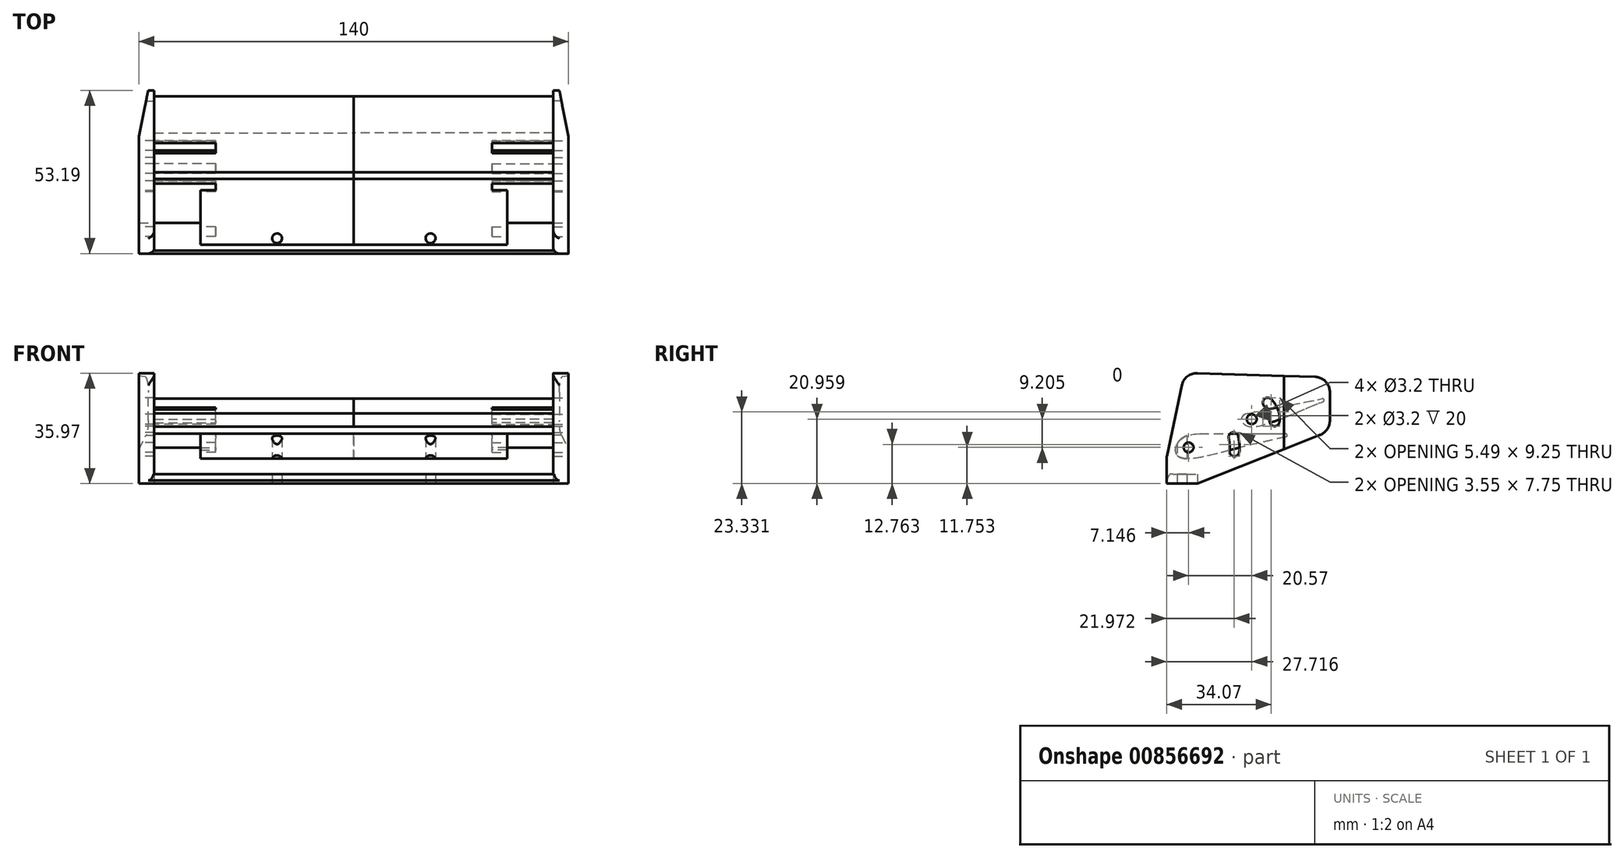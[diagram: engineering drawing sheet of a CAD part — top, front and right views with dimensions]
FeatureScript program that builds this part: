
annotation { "Feature Type Name" : "Feature", "Feature Type Description" : "" }
export const myFeature = defineFeature(function(context is Context, id is Id, definition is map)
    precondition{}
    {
        {
            var Q0;
            Q0=qCreatedBy(makeId("Right.planeOp"),FACE);
            var sketch = newSketch(context, id + "F0", { "sketchPlane" : qUnion([Q0])});
            skFitSpline(sketch, "E0", {"points": [v(0, 15) * mm, v(-15.97, 11.3) * mm, v(-26.3, 8.63) * mm, v(-36.38, 6.87) * mm, v(-40, 8.6) * mm, v(-38.45, 13.22) * mm, v(-32.23, 15) * mm], "startDerivative": vector(-50.3, -12.86) * mm, "endDerivative": vector(44.03, 0) * mm});
            skLineSegment(sketch, "E1", {"start": v(-32.23, 15) * mm, "end": v(-4.23, 15) * mm});
            skArc(sketch, "E2.filletArc", {"start": v(-4.11, 14.01) * mm, "mid": v(-3.73, 14.56) * mm, "end": v(-4.23, 15) * mm});
            skSolve(sketch);
        }
        {
            var Q0;
            Q0 = qSketchRegion(id + "F0", true);
            extrude(context, id + "F1", {"entities" : qUnion([Q0]), "depth" : 65 * mm, "offsetDistance" : 25 * mm});
        }
        {
            var Q0;
            Q0=makeQuery(id+"F1.opExtrude","CAP_FACE",FACE,{"disambiguationData":[OSD([sQuery(id+"F0.wireOp",EDGE,"E0"),sQuery(id+"F0.wireOp",EDGE,"E1"),sQuery(id+"F0.wireOp",EDGE,"E2.filletArc")])],"isStart":false});
            var sketch = newSketch(context, id + "F2", { "sketchPlane" : qUnion([Q0])});
            skCircle(sketch, "E3", {"center": v(-35.87, 10.53) * mm, "radius": 1.5 * mm});
            skSolve(sketch);
        }
        {
            var Q0;
            Q0 = qSketchRegion(id + "F2", true);
            extrude(context, id + "F3", {"entities" : qUnion([Q0]), "operationType" : NewBodyOperationType.REMOVE, "endBound" : BoundingType.SYMMETRIC, "oppositeDirection" : true, "depth" : 20 * mm, "offsetDistance" : 25 * mm});
        }
        {
            var Q0;
            Q0=qCreatedBy(makeId("Right.planeOp"),FACE);
            var sketch = newSketch(context, id + "F4", { "sketchPlane" : qUnion([Q0])});
            skLineSegment(sketch, "E4", {"start": v(-16.48, 21.66) * mm, "end": v(12.95, 27.47) * mm});
            skFitSpline(sketch, "E5", {"points": [v(-16.48, 21.66) * mm, v(-18.42, 20.57) * mm, v(-18.54, 19.05) * mm, v(-16.42, 17.47) * mm, v(-12.4, 17.65) * mm, v(-5.18, 20.08) * mm, v(4.36, 24.03) * mm, v(12.95, 27.47) * mm], "startDerivative": vector(-25.21, -3.34) * mm, "endDerivative": vector(44.37, 18.22) * mm});
            skSolve(sketch);
        }
        {
            var Q0;
            Q0 = qSketchRegion(id + "F4", true);
            extrude(context, id + "F5", {"entities" : qUnion([Q0]), "depth" : 65 * mm, "offsetDistance" : 25 * mm});
        }
        {
            var Q0;
            {var subQ0=sQuery(id+"F4.wireOp",EDGE,"E5");var subQ1=sQuery(id+"F4.wireOp",EDGE,"E4");Q0=makeQuery(id+"F5.opExtrude","SWEPT_EDGE",EDGE,{"disambiguationData":[OSD([subQ1,subQ0]),TDD([makeQuery(id+"F4.imprint","INTERSECT",VERTEX,{"disambiguationData":[OD(1.0)],"derivedFrom":[subQ1,subQ0]})])]});}
            fillet(context, id + "F6", {"entities" : qUnion([Q0]), "radius" : .5 * mm, "tangentPropagation" : true, "allowEdgeOverflow" : false});
        }
        {
            var Q0;
            Q0=makeQuery(id+"F5.opExtrude","CAP_FACE",FACE,{"disambiguationData":[OSD([sQuery(id+"F4.wireOp",EDGE,"E4"),sQuery(id+"F4.wireOp",EDGE,"E5")])],"isStart":false});
            var sketch = newSketch(context, id + "F7", { "sketchPlane" : qUnion([Q0])});
            skCircle(sketch, "E6", {"center": v(-15.3, 19.74) * mm, "radius": 1.5 * mm});
            skSolve(sketch);
        }
        {
            var Q0;
            Q0 = qSketchRegion(id + "F7", true);
            extrude(context, id + "F8", {"entities" : qUnion([Q0]), "operationType" : NewBodyOperationType.REMOVE, "endBound" : BoundingType.SYMMETRIC, "oppositeDirection" : true, "depth" : 15 * mm, "offsetDistance" : 25 * mm});
        }
        {
            var Q0;
            Q0=makeQuery(id+"F5.opExtrude","CAP_FACE",FACE,{"disambiguationData":[OSD([sQuery(id+"F4.wireOp",EDGE,"E4"),sQuery(id+"F4.wireOp",EDGE,"E5")])],"isStart":false});
            var sketch = newSketch(context, id + "F9", { "sketchPlane" : qUnion([Q0])});
            skLineSegment(sketch, "E7", {"start": v(-44.19, 1.78) * mm, "end": v(-33.46, 1.78) * mm});
            skLineSegment(sketch, "E8", {"start": v(-33.46, 1.78) * mm, "end": v(10.17, 15.63) * mm});
            skLineSegment(sketch, "E9", {"start": v(10.17, 15.63) * mm, "end": v(10.17, 33.4) * mm});
            skLineSegment(sketch, "E10", {"start": v(-39.8, 22.63) * mm, "end": v(-44.19, 1.78) * mm});
            skLineSegment(sketch, "E11", {"start": v(-39.8, 22.63) * mm, "end": v(-37.21, 34.88) * mm});
            skLineSegment(sketch, "E12", {"start": v(-37.21, 34.88) * mm, "end": v(10.17, 33.4) * mm});
            skSolve(sketch);
        }
        {
            var Q0;
            Q0 = qSketchRegion(id + "F9", true);
            extrude(context, id + "F10", {"entities" : qUnion([Q0]), "depth" : 5 * mm, "offsetDistance" : 25 * mm});
        }
        {
            var Q0;
            Q0=makeQuery(id+"F10.opExtrude","SWEPT_EDGE",EDGE,{"disambiguationData":[OSD([sQuery(id+"F9.wireOp",EDGE,"ADhL9wM5-Wbhb-7g79-Ji5l-QH4fZ3eOvgQA"),sQuery(id+"F9.wireOp",EDGE,"E10")])]});
            fillet(context, id + "F11", {"entities" : qUnion([Q0]), "radius" : 5 * mm, "tangentPropagation" : true, "allowEdgeOverflow" : false});
        }
        {
            var Q0;
            Q0=makeQuery(id+"F10.opExtrude","SWEPT_EDGE",EDGE,{"disambiguationData":[OSD([sQuery(id+"F9.wireOp",EDGE,"E9"),sQuery(id+"F9.wireOp",EDGE,"ADhL9wM5-Wbhb-7g79-Ji5l-QH4fZ3eOvgQA")])]});
            var Q1;
            Q1=makeQuery(id+"F10.opExtrude","SWEPT_EDGE",EDGE,{"disambiguationData":[OSD([sQuery(id+"F9.wireOp",EDGE,"E8"),sQuery(id+"F9.wireOp",EDGE,"E9")])]});
            var Q2;
            Q2=makeQuery(id+"F10.opExtrude","SWEPT_EDGE",EDGE,{"disambiguationData":[OSD([sQuery(id+"F9.wireOp",EDGE,"E7"),sQuery(id+"F9.wireOp",EDGE,"E8")])]});
            fillet(context, id + "F12", {"entities" : qUnion([Q0, Q1, Q2]), "radius" : 5 * mm, "tangentPropagation" : true, "allowEdgeOverflow" : false});
        }
        {
            var Q0;
            Q0=makeQuery(id+"F10.opExtrude","CAP_FACE",FACE,{"disambiguationData":[OSD([sQuery(id+"F9.wireOp",EDGE,"E7"),sQuery(id+"F9.wireOp",EDGE,"E8"),sQuery(id+"F9.wireOp",EDGE,"E9"),sQuery(id+"F9.wireOp",EDGE,"ADhL9wM5-Wbhb-7g79-Ji5l-QH4fZ3eOvgQA"),sQuery(id+"F9.wireOp",EDGE,"E10")])],"isStart":false});
            var sketch = newSketch(context, id + "F13", { "sketchPlane" : qUnion([Q0])});
            skCircle(sketch, "E13.0", {"center": v(-15.3, 19.74) * mm, "radius": 1.6 * mm});
            skArc(sketch, "E14", {"start": v(-8.98, 26.28) * mm, "mid": v(-11.25, 26.25) * mm, "end": v(-11.2, 23.98) * mm});
            skArc(sketch, "E15", {"start": v(-9.43, 19.22) * mm, "mid": v(-7.97, 17.49) * mm, "end": v(-6.24, 18.94) * mm});
            skArc(sketch, "E16", {"start": v(-9.43, 19.22) * mm, "mid": v(-9.78, 21.8) * mm, "end": v(-11.2, 23.98) * mm});
            skArc(sketch, "E17", {"start": v(-6.24, 18.94) * mm, "mid": v(-6.78, 22.92) * mm, "end": v(-8.98, 26.28) * mm});
            skSolve(sketch);
        }
        {
            var Q0;
            Q0 = qSketchRegion(id + "F13", true);
            extrude(context, id + "F14", {"entities" : qUnion([Q0]), "operationType" : NewBodyOperationType.REMOVE, "oppositeDirection" : true, "depth" : 25 * mm, "offsetDistance" : 25 * mm});
        }
        {
            var Q0;
            Q0=makeQuery(id+"F10.opExtrude","CAP_FACE",FACE,{"disambiguationData":[OSD([sQuery(id+"F9.wireOp",EDGE,"E7"),sQuery(id+"F9.wireOp",EDGE,"E8"),sQuery(id+"F9.wireOp",EDGE,"E9"),sQuery(id+"F9.wireOp",EDGE,"ADhL9wM5-Wbhb-7g79-Ji5l-QH4fZ3eOvgQA"),sQuery(id+"F9.wireOp",EDGE,"E10")])],"isStart":false});
            var sketch = newSketch(context, id + "F15", { "sketchPlane" : qUnion([Q0])});
            skCircle(sketch, "E18.0", {"center": v(-35.87, 10.53) * mm, "radius": 1.5 * mm, "construction": true});
            skCircle(sketch, "E19", {"center": v(-35.87, 10.53) * mm, "radius": 1.6 * mm});
            skArc(sketch, "E20", {"start": v(-19.68, 14.2) * mm, "mid": v(-21.6, 15.4) * mm, "end": v(-22.8, 13.49) * mm});
            skArc(sketch, "E21", {"start": v(-22.52, 9.4) * mm, "mid": v(-21.06, 7.67) * mm, "end": v(-19.33, 9.13) * mm});
            skArc(sketch, "E22", {"start": v(-22.52, 9.4) * mm, "mid": v(-22.5, 11.45) * mm, "end": v(-22.8, 13.49) * mm});
            skArc(sketch, "E23", {"start": v(-19.33, 9.13) * mm, "mid": v(-19.31, 11.67) * mm, "end": v(-19.68, 14.2) * mm});
            skSolve(sketch);
        }
        {
            var Q0;
            Q0 = qSketchRegion(id + "F15", true);
            extrude(context, id + "F16", {"entities" : qUnion([Q0]), "operationType" : NewBodyOperationType.REMOVE, "oppositeDirection" : true, "depth" : 25 * mm, "offsetDistance" : 25 * mm});
        }
        {
            var Q0;
            Q0=makeQuery(id+"F1.opExtrude","CAP_FACE",FACE,{"disambiguationData":[OSD([sQuery(id+"F0.wireOp",EDGE,"E0"),sQuery(id+"F0.wireOp",EDGE,"E1"),sQuery(id+"F0.wireOp",EDGE,"E2.filletArc")])],"isStart":false});
            var sketch = newSketch(context, id + "F17", { "sketchPlane" : qUnion([Q0])});
            skArc(sketch, "E24.0", {"start": v(-19.68, 14.2) * mm, "mid": v(-21.6, 15.4) * mm, "end": v(-22.8, 13.49) * mm});
            skCircle(sketch, "E25", {"center": v(-35.87, 10.53) * mm, "radius": 15 * mm});
            skCircle(sketch, "E26", {"center": v(-21.02, 12.64) * mm, "radius": 1.5 * mm});
            skSolve(sketch);
        }
        {
            var Q0;
            {var subQ0=sQuery(id+"F17.wireOp",EDGE,"E26");var subQ1=sQuery(id+"F17.wireOp",EDGE,"E25");var subQ2=makeQuery(id+"F17.imprint","INTERSECT",VERTEX,{"disambiguationData":[OD(0.0)],"derivedFrom":[subQ1,subQ0]});Q0=makeQuery(id+"F17.imprint","IMPRINT",FACE,{"disambiguationData":[TD([[makeQuery(id+"F17.imprint","IMPRINT",EDGE,{"disambiguationData":[TD([[subQ2,1.0]])],"derivedFrom":subQ1}),-1.0]])]});}
            var Q1;
            {var subQ0=sQuery(id+"F17.wireOp",EDGE,"E26");var subQ1=sQuery(id+"F17.wireOp",EDGE,"E25");var subQ2=makeQuery(id+"F17.imprint","INTERSECT",VERTEX,{"disambiguationData":[OD(0.0)],"derivedFrom":[subQ1,subQ0]});Q1=makeQuery(id+"F17.imprint","IMPRINT",FACE,{"disambiguationData":[TD([[makeQuery(id+"F17.imprint","IMPRINT",EDGE,{"disambiguationData":[TD([[subQ2,1.0]])],"derivedFrom":subQ1}),1.0]])]});}
            var Q2;
            Q2=sQuery(id+"F17.wireOp",EDGE,"E26");
            extrude(context, id + "F18", {"entities" : qUnion([Q0, Q1]), "operationType" : NewBodyOperationType.REMOVE, "surfaceEntities" : qUnion([Q2]), "oppositeDirection" : true, "depth" : 15 * mm, "offsetDistance" : 25 * mm});
        }
        {
            var Q0;
            Q0=makeQuery(id+"F5.opExtrude","CAP_FACE",FACE,{"disambiguationData":[OSD([sQuery(id+"F4.wireOp",EDGE,"E4"),sQuery(id+"F4.wireOp",EDGE,"E5")])],"isStart":false});
            var sketch = newSketch(context, id + "F19", { "sketchPlane" : qUnion([Q0])});
            skPoint(sketch, "E27.0", {"position": v(-11.25, 26.25) * mm});
            skCircle(sketch, "E28", {"center": v(-7.98, 21.37) * mm, "radius": 1.5 * mm});
            skSolve(sketch);
        }
        {
            var Q0;
            Q0 = qSketchRegion(id + "F19", true);
            extrude(context, id + "F20", {"entities" : qUnion([Q0]), "operationType" : NewBodyOperationType.REMOVE, "oppositeDirection" : true, "depth" : 15 * mm, "offsetDistance" : 25 * mm});
        }
        {
            var Q0;
            Q0=makeQuery(id+"F1.opExtrude","SWEPT_BODY",BODY,{"disambiguationData":[OSD([sQuery(id+"F0.wireOp",EDGE,"E0"),sQuery(id+"F0.wireOp",EDGE,"E1"),sQuery(id+"F0.wireOp",EDGE,"E2.filletArc")])]});
            var Q1;
            Q1=makeQuery(id+"F5.opExtrude","SWEPT_BODY",BODY,{"disambiguationData":[OSD([sQuery(id+"F4.wireOp",EDGE,"E4"),sQuery(id+"F4.wireOp",EDGE,"E5")])]});
            var Q2;
            Q2=qCreatedBy(makeId("Right.planeOp"),FACE);
            mirror(context, id + "F21", {"entities" : qUnion([Q0, Q1]), "mirrorPlane" : qUnion([Q2])});
        }
        {
            var Q0;
            Q0=makeQuery(id+"F10.opExtrude","SWEPT_BODY",BODY,{"disambiguationData":[OSD([sQuery(id+"F9.wireOp",EDGE,"E7"),sQuery(id+"F9.wireOp",EDGE,"E8"),sQuery(id+"F9.wireOp",EDGE,"E9"),sQuery(id+"F9.wireOp",EDGE,"ADhL9wM5-Wbhb-7g79-Ji5l-QH4fZ3eOvgQA"),sQuery(id+"F9.wireOp",EDGE,"E10")])]});
            var Q1;
            Q1=qCreatedBy(makeId("Right.planeOp"),FACE);
            mirror(context, id + "F22", {"entities" : qUnion([Q0]), "mirrorPlane" : qUnion([Q1])});
        }
        {
            var Q0;
            Q0=makeQuery(id+"F10.opExtrude","SWEPT_EDGE",EDGE,{"disambiguationData":[OSD([sQuery(id+"F9.wireOp",EDGE,"E11"),sQuery(id+"F9.wireOp",EDGE,"E12")])]});
            fillet(context, id + "F23", {"entities" : qUnion([Q0]), "radius" : 5 * mm, "tangentPropagation" : true, "allowEdgeOverflow" : false});
        }
        {
            var Q0;
            Q0=makeQuery(id+"F22.opPattern","COPY",EDGE,{"derivedFrom":makeQuery(id+"F10.opExtrude","SWEPT_EDGE",EDGE,{"disambiguationData":[OSD([sQuery(id+"F9.wireOp",EDGE,"E11"),sQuery(id+"F9.wireOp",EDGE,"E12")])]}),"instanceName":"1"});
            fillet(context, id + "F24", {"entities" : qUnion([Q0]), "radius" : 5 * mm, "tangentPropagation" : true, "allowEdgeOverflow" : false});
        }
        {
            var Q0;
            Q0=makeQuery(id+"F22.opPattern","COPY",FACE,{"derivedFrom":makeQuery(id+"F10.opExtrude","SWEPT_FACE",FACE,{"disambiguationData":[OSD([sQuery(id+"F9.wireOp",EDGE,"E7")])]}),"instanceName":"1"});
            var sketch = newSketch(context, id + "F25", { "sketchPlane" : qUnion([Q0])});
            skLineSegment(sketch, "E29", {"start": v(-70, 43.02) * mm, "end": v(70, 43.02) * mm});
            skLineSegment(sketch, "E30.0", {"start": v(70, 43.02) * mm, "end": v(70, -6.68) * mm});
            skPoint(sketch, "E31.orphan", {"position": v(70, 32.72) * mm});
            skLineSegment(sketch, "E32.0", {"start": v(-70, 43.02) * mm, "end": v(-70, -6.68) * mm});
            skPoint(sketch, "E33.orphan", {"position": v(-70, 32.72) * mm});
            skLineSegment(sketch, "E34.0", {"start": v(-70, 33.02) * mm, "end": v(70, 33.02) * mm});
            skSolve(sketch);
        }
        {
            var Q0;
            Q0 = qSketchRegion(id + "F25", true);
            extrude(context, id + "F26", {"entities" : qUnion([Q0]), "operationType" : NewBodyOperationType.ADD, "depth" : 3 * mm, "offsetDistance" : 25 * mm});
        }
        {
            var Q0;
            Q0=makeQuery(id+"F26.boolean.opBoolean","MERGE",FACE,{"derivedFrom":[makeQuery(id+"F10.opExtrude","CAP_FACE",FACE,{"disambiguationData":[OSD([sQuery(id+"F9.wireOp",EDGE,"E7"),sQuery(id+"F9.wireOp",EDGE,"E8"),sQuery(id+"F9.wireOp",EDGE,"E9"),sQuery(id+"F9.wireOp",EDGE,"E10"),sQuery(id+"F9.wireOp",EDGE,"E11"),sQuery(id+"F9.wireOp",EDGE,"E12")])],"isStart":false}),makeQuery(id+"F26.opExtrude","SWEPT_FACE",FACE,{"disambiguationData":[OSD([sQuery(id+"F25.wireOp",EDGE,"E30.0")])]})]});
            var sketch = newSketch(context, id + "F27", { "sketchPlane" : qUnion([Q0])});
            skLineSegment(sketch, "E35", {"start": v(-33.02, -1.22) * mm, "end": v(6.68, 14.52) * mm});
            skLineSegment(sketch, "E36.0", {"start": v(-33.02, -1.22) * mm, "end": v(-33.02, 1.78) * mm});
            skLineSegment(sketch, "E37.0", {"start": v(-34.23, 1.78) * mm, "end": v(-33.02, 1.78) * mm});
            skArc(sketch, "E38.0", {"start": v(-34.23, 1.78) * mm, "mid": v(-33.47, 1.84) * mm, "end": v(-32.72, 2.02) * mm});
            skLineSegment(sketch, "E39.0", {"start": v(-32.72, 2.02) * mm, "end": v(6.68, 14.52) * mm});
            skArc(sketch, "E40.0", {"start": v(-42.92, 7.82) * mm, "mid": v(-41.9, 3.63) * mm, "end": v(-38.02, 1.78) * mm});
            skLineSegment(sketch, "E41.0", {"start": v(-43.02, 1.78) * mm, "end": v(-38.02, 1.78) * mm});
            skLineSegment(sketch, "E42", {"start": v(-43.02, 1.78) * mm, "end": v(-43.02, 6.78) * mm});
            skSolve(sketch);
        }
        {
            var Q0;
            Q0 = qSketchRegion(id + "F27", true);
            var Q1;
            Q1=makeQuery(id+"F10.opExtrude","CAP_FACE",FACE,{"disambiguationData":[OSD([sQuery(id+"F9.wireOp",EDGE,"E7"),sQuery(id+"F9.wireOp",EDGE,"E8"),sQuery(id+"F9.wireOp",EDGE,"E9"),sQuery(id+"F9.wireOp",EDGE,"E10"),sQuery(id+"F9.wireOp",EDGE,"E11"),sQuery(id+"F9.wireOp",EDGE,"E12")])],"isStart":true});
            extrude(context, id + "F28", {"entities" : qUnion([Q0]), "endBound" : BoundingType.UP_TO_SURFACE, "oppositeDirection" : true, "depth" : 25 * mm, "endBoundEntityFace" : qUnion([Q1]), "offsetDistance" : 25 * mm});
        }
        {
            var Q0;
            Q0=makeQuery(id+"F28.opExtrude","SWEPT_BODY",BODY,{"disambiguationData":[OSD([sQuery(id+"F27.wireOp",EDGE,"E40.0"),sQuery(id+"F27.wireOp",EDGE,"E41.0"),sQuery(id+"F27.wireOp",EDGE,"E42")])]});
            var Q1;
            Q1=makeQuery(id+"F28.opExtrude","SWEPT_BODY",BODY,{"disambiguationData":[OSD([sQuery(id+"F27.wireOp",EDGE,"E35"),sQuery(id+"F27.wireOp",EDGE,"E36.0"),sQuery(id+"F27.wireOp",EDGE,"E37.0"),sQuery(id+"F27.wireOp",EDGE,"E38.0"),sQuery(id+"F27.wireOp",EDGE,"E39.0")])]});
            var Q2;
            Q2=qCreatedBy(makeId("Right.planeOp"),FACE);
            mirror(context, id + "F29", {"operationType" : NewBodyOperationType.ADD, "entities" : qUnion([Q0, Q1]), "mirrorPlane" : qUnion([Q2])});
        }
        {
            var Q0;
            Q0=makeQuery(id+"F26.opExtrude","CAP_FACE",FACE,{"disambiguationData":[OSD([sQuery(id+"F25.wireOp",EDGE,"E29"),sQuery(id+"F25.wireOp",EDGE,"E30.0"),sQuery(id+"F25.wireOp",EDGE,"E32.0"),sQuery(id+"F25.wireOp",EDGE,"E34.0")])],"isStart":false});
            var sketch = newSketch(context, id + "F30", { "sketchPlane" : qUnion([Q0])});
            skCircle(sketch, "E43", {"center": v(-25, 38.02) * mm, "radius": 1.6 * mm});
            skCircle(sketch, "E44.MirrorC", {"center": v(25, 38.02) * mm, "radius": 1.6 * mm});
            skSolve(sketch);
        }
        {
            var Q0;
            Q0 = qSketchRegion(id + "F30", true);
            extrude(context, id + "F31", {"entities" : qUnion([Q0]), "operationType" : NewBodyOperationType.REMOVE, "oppositeDirection" : true, "depth" : 25 * mm, "offsetDistance" : 25 * mm});
        }
        {
            var Q0;
            Q0=makeQuery(id+"F26.opExtrude","CAP_EDGE",EDGE,{"disambiguationData":[OSD([sQuery(id+"F25.wireOp",EDGE,"E29")])],"isStart":true});
            chamfer(context, id + "F32", {"entities" : qUnion([Q0]), "chamferType" : ChamferType.TWO_OFFSETS, "width1" : 1 * mm, "oppositeDirection" : false, "width2" : 2 * mm, "tangentPropagation" : true});
        }
        {
            var Q0;
            Q0=makeQuery(id+"F10.opExtrude","CAP_EDGE",EDGE,{"disambiguationData":[OSD([sQuery(id+"F9.wireOp",EDGE,"E10"),sQuery(id+"F9.wireOp",EDGE,"E11")])],"isStart":true});
            var Q1;
            Q1=makeQuery(id+"F28.opExtrude","CAP_EDGE",EDGE,{"disambiguationData":[OSD([sQuery(id+"F27.wireOp",EDGE,"E42")])],"isStart":false});
            var Q2;
            {var subQ0=sQuery(id+"F9.wireOp",EDGE,"E10");var subQ1=sQuery(id+"F9.wireOp",EDGE,"E7");Q2=makeQuery(id+"F11.opFillet","BLEND_EDGE",EDGE,{"blendedFrom":[makeQuery(id+"F10.opExtrude","SWEPT_EDGE",EDGE,{"disambiguationData":[OSD([subQ1,subQ0])]}),makeQuery(id+"F10.opExtrude","CAP_FACE",FACE,{"disambiguationData":[OSD([subQ1,sQuery(id+"F9.wireOp",EDGE,"E8"),sQuery(id+"F9.wireOp",EDGE,"E9"),subQ0,sQuery(id+"F9.wireOp",EDGE,"E11"),sQuery(id+"F9.wireOp",EDGE,"E12")])],"isStart":true})],"blendedInto":[makeQuery(id+"F10.opExtrude","CAP_FACE",FACE,{"disambiguationData":[OSD([subQ1,sQuery(id+"F9.wireOp",EDGE,"E8"),sQuery(id+"F9.wireOp",EDGE,"E9"),subQ0,sQuery(id+"F9.wireOp",EDGE,"E11"),sQuery(id+"F9.wireOp",EDGE,"E12")])],"isStart":true})]});}
            var Q3;
            Q3=makeQuery(id+"F22.opPattern","COPY",EDGE,{"derivedFrom":makeQuery(id+"F10.opExtrude","CAP_EDGE",EDGE,{"disambiguationData":[OSD([sQuery(id+"F9.wireOp",EDGE,"E10"),sQuery(id+"F9.wireOp",EDGE,"E11")])],"isStart":true}),"instanceName":"1"});
            var Q4;
            Q4=makeQuery(id+"F29.opPattern","COPY",EDGE,{"derivedFrom":makeQuery(id+"F28.opExtrude","CAP_EDGE",EDGE,{"disambiguationData":[OSD([sQuery(id+"F27.wireOp",EDGE,"E42")])],"isStart":false}),"instanceName":"1"});
            var Q5;
            {var subQ0=sQuery(id+"F9.wireOp",EDGE,"E10");var subQ1=sQuery(id+"F9.wireOp",EDGE,"E7");Q5=makeQuery(id+"F22.opPattern","COPY",EDGE,{"derivedFrom":makeQuery(id+"F11.opFillet","BLEND_EDGE",EDGE,{"blendedFrom":[makeQuery(id+"F10.opExtrude","SWEPT_EDGE",EDGE,{"disambiguationData":[OSD([subQ1,subQ0])]}),makeQuery(id+"F10.opExtrude","CAP_FACE",FACE,{"disambiguationData":[OSD([subQ1,sQuery(id+"F9.wireOp",EDGE,"E8"),sQuery(id+"F9.wireOp",EDGE,"E9"),subQ0,sQuery(id+"F9.wireOp",EDGE,"E11"),sQuery(id+"F9.wireOp",EDGE,"E12")])],"isStart":true})],"blendedInto":[makeQuery(id+"F10.opExtrude","CAP_FACE",FACE,{"disambiguationData":[OSD([subQ1,sQuery(id+"F9.wireOp",EDGE,"E8"),sQuery(id+"F9.wireOp",EDGE,"E9"),subQ0,sQuery(id+"F9.wireOp",EDGE,"E11"),sQuery(id+"F9.wireOp",EDGE,"E12")])],"isStart":true})]}),"instanceName":"1"});}
            fillet(context, id + "F33", {"entities" : qUnion([Q0, Q1, Q2, Q3, Q4, Q5]), "radius" : 2 * mm, "allowEdgeOverflow" : false});
        }
        {
            var Q0;
            Q0=makeQuery(id+"F22.opPattern","COPY",EDGE,{"derivedFrom":makeQuery(id+"F10.opExtrude","CAP_EDGE",EDGE,{"disambiguationData":[OSD([sQuery(id+"F9.wireOp",EDGE,"E9")])],"isStart":false}),"instanceName":"1"});
            chamfer(context, id + "F34", {"entities" : qUnion([Q0]), "chamferType" : ChamferType.TWO_OFFSETS, "width1" : 3 * mm, "oppositeDirection" : false, "width2" : 15 * mm});
        }
        {
            var Q0;
            Q0=makeQuery(id+"F10.opExtrude","CAP_EDGE",EDGE,{"disambiguationData":[OSD([sQuery(id+"F9.wireOp",EDGE,"E9")])],"isStart":false});
            chamfer(context, id + "F35", {"entities" : qUnion([Q0]), "chamferType" : ChamferType.TWO_OFFSETS, "width1" : 15 * mm, "oppositeDirection" : false, "width2" : 3 * mm});
        }
    });
